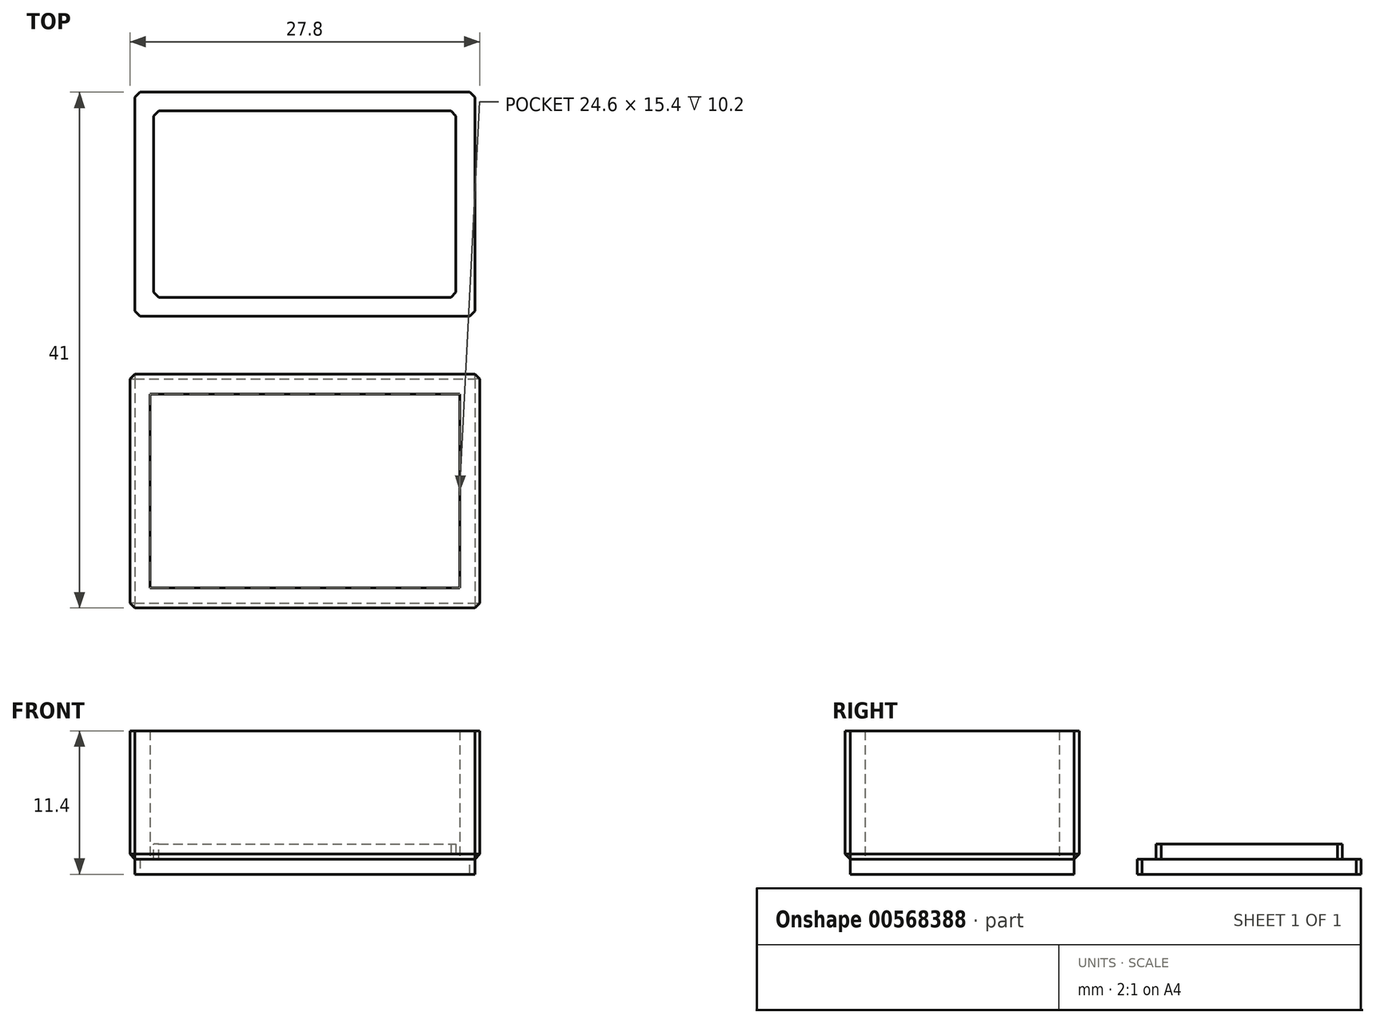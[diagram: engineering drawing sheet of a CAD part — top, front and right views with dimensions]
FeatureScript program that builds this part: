
annotation { "Feature Type Name" : "Feature", "Feature Type Description" : "" }
export const myFeature = defineFeature(function(context is Context, id is Id, definition is map)
    precondition{}
    {
        {
            var Q0;
            Q0=qCreatedBy(makeId("Top.planeOp"),FACE);
            var sketch = newSketch(context, id + "F0", { "sketchPlane" : qUnion([Q0])});
            skLineSegment(sketch, "E0.bottom", {"start": v(-13.5, 8.9) * mm, "end": v(13.5, 8.9) * mm});
            skLineSegment(sketch, "E0.top", {"start": v(-13.5, -8.9) * mm, "end": v(13.5, -8.9) * mm});
            skLineSegment(sketch, "E0.left", {"start": v(-13.5, 8.9) * mm, "end": v(-13.5, -8.9) * mm});
            skLineSegment(sketch, "E0.right", {"start": v(13.5, 8.9) * mm, "end": v(13.5, -8.9) * mm});
            skPoint(sketch, "E0.middle", {"position": v(0, 0) * mm});
            skLineSegment(sketch, "E1.bottom", {"start": v(13.5, 13.9) * mm, "end": v(-13.5, 13.9) * mm});
            skLineSegment(sketch, "E1.top", {"start": v(13.5, 31.7) * mm, "end": v(-13.5, 31.7) * mm});
            skLineSegment(sketch, "E1.left", {"start": v(13.5, 13.9) * mm, "end": v(13.5, 31.7) * mm});
            skLineSegment(sketch, "E1.right", {"start": v(-13.5, 13.9) * mm, "end": v(-13.5, 31.7) * mm});
            skPoint(sketch, "E1.middle", {"position": v(0, 22.8) * mm});
            skSolve(sketch);
        }
        {
            var Q0;
            Q0 = qSketchRegion(id + "F0", true);
            extrude(context, id + "F1", {"entities" : qUnion([Q0]), "depth" : 1.2 * mm, "offsetDistance" : 25 * mm});
        }
        {
            var Q0;
            Q0=makeQuery(id+"F1.opExtrude","CAP_FACE",FACE,{"disambiguationData":[OSD([sQuery(id+"F0.wireOp",EDGE,"E0.bottom"),sQuery(id+"F0.wireOp",EDGE,"E0.top"),sQuery(id+"F0.wireOp",EDGE,"E0.left"),sQuery(id+"F0.wireOp",EDGE,"E0.right")])],"isStart":false});
            var sketch = newSketch(context, id + "F2", { "sketchPlane" : qUnion([Q0])});
            skLineSegment(sketch, "E2.bottom", {"start": v(-12.3, 7.7) * mm, "end": v(12.3, 7.7) * mm});
            skLineSegment(sketch, "E2.top", {"start": v(-12.3, -7.7) * mm, "end": v(12.3, -7.7) * mm});
            skLineSegment(sketch, "E2.left", {"start": v(-12.3, 7.7) * mm, "end": v(-12.3, -7.7) * mm});
            skLineSegment(sketch, "E2.right", {"start": v(12.3, 7.7) * mm, "end": v(12.3, -7.7) * mm});
            skPoint(sketch, "E2.middle", {"position": v(0, 0) * mm});
            skLineSegment(sketch, "E3.bottom", {"start": v(-13.5, 8.9) * mm, "end": v(13.5, 8.9) * mm});
            skLineSegment(sketch, "E3.top", {"start": v(-13.5, -8.9) * mm, "end": v(13.5, -8.9) * mm});
            skLineSegment(sketch, "E3.left", {"start": v(-13.5, 8.9) * mm, "end": v(-13.5, -8.9) * mm});
            skLineSegment(sketch, "E3.right", {"start": v(13.5, 8.9) * mm, "end": v(13.5, -8.9) * mm});
            skLineSegment(sketch, "E4.bottom", {"start": v(-13.9, 9.3) * mm, "end": v(13.9, 9.3) * mm});
            skLineSegment(sketch, "E4.top", {"start": v(-13.9, -9.3) * mm, "end": v(13.9, -9.3) * mm});
            skLineSegment(sketch, "E4.left", {"start": v(-13.9, 9.3) * mm, "end": v(-13.9, -9.3) * mm});
            skLineSegment(sketch, "E4.right", {"start": v(13.9, 9.3) * mm, "end": v(13.9, -9.3) * mm});
            skSolve(sketch);
        }
        {
            var Q0;
            Q0=makeQuery(id+"F2.imprint","IMPRINT",FACE,{"disambiguationData":[TD([[makeQuery(id+"F2.imprint","IMPRINT",EDGE,{"derivedFrom":sQuery(id+"F2.wireOp",EDGE,"E2.bottom")}),1.0]])]});
            var Q1;
            Q1=makeQuery(id+"F2.imprint","IMPRINT",FACE,{"disambiguationData":[TD([[makeQuery(id+"F2.imprint","IMPRINT",EDGE,{"derivedFrom":sQuery(id+"F2.wireOp",EDGE,"E3.bottom")}),1.0]])]});
            extrude(context, id + "F3", {"entities" : qUnion([Q0, Q1]), "operationType" : NewBodyOperationType.ADD, "depth" : 10.2 * mm, "offsetDistance" : 25 * mm});
        }
        {
            var Q0;
            Q0=makeQuery(id+"F1.opExtrude","CAP_FACE",FACE,{"disambiguationData":[OSD([sQuery(id+"F0.wireOp",EDGE,"E1.bottom"),sQuery(id+"F0.wireOp",EDGE,"E1.top"),sQuery(id+"F0.wireOp",EDGE,"E1.left"),sQuery(id+"F0.wireOp",EDGE,"E1.right")])],"isStart":false});
            var sketch = newSketch(context, id + "F4", { "sketchPlane" : qUnion([Q0])});
            skLineSegment(sketch, "E5.bottom", {"start": v(-12, 30.2) * mm, "end": v(12, 30.2) * mm});
            skLineSegment(sketch, "E5.top", {"start": v(-12, 15.4) * mm, "end": v(12, 15.4) * mm});
            skLineSegment(sketch, "E5.left", {"start": v(-12, 30.2) * mm, "end": v(-12, 15.4) * mm});
            skLineSegment(sketch, "E5.right", {"start": v(12, 30.2) * mm, "end": v(12, 15.4) * mm});
            skPoint(sketch, "E5.middle", {"position": v(0, 22.8) * mm});
            skSolve(sketch);
        }
        {
            var Q0;
            Q0=makeQuery(id+"F4.imprint","IMPRINT",FACE,{"disambiguationData":[TD([[makeQuery(id+"F4.imprint","IMPRINT",EDGE,{"derivedFrom":sQuery(id+"F4.wireOp",EDGE,"E5.bottom")}),-1.0]])]});
            extrude(context, id + "F5", {"entities" : qUnion([Q0]), "operationType" : NewBodyOperationType.ADD, "depth" : 1.2 * mm, "offsetDistance" : 25 * mm});
        }
        {
            var Q0;
            Q0=makeQuery(id+"F3.opExtrude","CAP_EDGE",EDGE,{"disambiguationData":[OSD([sQuery(id+"F2.wireOp",EDGE,"E4.left")])],"isStart":true});
            var Q1;
            Q1=makeQuery(id+"F3.opExtrude","SWEPT_EDGE",EDGE,{"disambiguationData":[OSD([sQuery(id+"F2.wireOp",EDGE,"E4.top"),sQuery(id+"F2.wireOp",EDGE,"E4.left")])]});
            var Q2;
            Q2=makeQuery(id+"F3.opExtrude","SWEPT_EDGE",EDGE,{"disambiguationData":[OSD([sQuery(id+"F2.wireOp",EDGE,"E4.bottom"),sQuery(id+"F2.wireOp",EDGE,"E4.left")])]});
            var Q3;
            Q3=makeQuery(id+"F3.opExtrude","SWEPT_EDGE",EDGE,{"disambiguationData":[OSD([sQuery(id+"F2.wireOp",EDGE,"E4.top"),sQuery(id+"F2.wireOp",EDGE,"E4.right")])]});
            var Q4;
            Q4=makeQuery(id+"F3.opExtrude","CAP_EDGE",EDGE,{"disambiguationData":[OSD([sQuery(id+"F2.wireOp",EDGE,"E4.right")])],"isStart":true});
            var Q5;
            Q5=makeQuery(id+"F3.opExtrude","SWEPT_EDGE",EDGE,{"disambiguationData":[OSD([sQuery(id+"F2.wireOp",EDGE,"E4.bottom"),sQuery(id+"F2.wireOp",EDGE,"E4.right")])]});
            var Q6;
            Q6=makeQuery(id+"F1.opExtrude","SWEPT_EDGE",EDGE,{"disambiguationData":[OSD([sQuery(id+"F0.wireOp",EDGE,"E1.top"),sQuery(id+"F0.wireOp",EDGE,"E1.left")])]});
            var Q7;
            Q7=makeQuery(id+"F5.opExtrude","SWEPT_EDGE",EDGE,{"disambiguationData":[OSD([sQuery(id+"F4.wireOp",EDGE,"E5.bottom"),sQuery(id+"F4.wireOp",EDGE,"E5.right")])]});
            var Q8;
            Q8=makeQuery(id+"F5.opExtrude","SWEPT_EDGE",EDGE,{"disambiguationData":[OSD([sQuery(id+"F4.wireOp",EDGE,"E5.top"),sQuery(id+"F4.wireOp",EDGE,"E5.right")])]});
            var Q9;
            Q9=makeQuery(id+"F1.opExtrude","SWEPT_EDGE",EDGE,{"disambiguationData":[OSD([sQuery(id+"F0.wireOp",EDGE,"E1.bottom"),sQuery(id+"F0.wireOp",EDGE,"E1.left")])]});
            var Q10;
            Q10=makeQuery(id+"F1.opExtrude","SWEPT_EDGE",EDGE,{"disambiguationData":[OSD([sQuery(id+"F0.wireOp",EDGE,"E1.top"),sQuery(id+"F0.wireOp",EDGE,"E1.right")])]});
            var Q11;
            Q11=makeQuery(id+"F5.opExtrude","SWEPT_EDGE",EDGE,{"disambiguationData":[OSD([sQuery(id+"F4.wireOp",EDGE,"E5.bottom"),sQuery(id+"F4.wireOp",EDGE,"E5.left")])]});
            var Q12;
            Q12=makeQuery(id+"F1.opExtrude","SWEPT_EDGE",EDGE,{"disambiguationData":[OSD([sQuery(id+"F0.wireOp",EDGE,"E1.bottom"),sQuery(id+"F0.wireOp",EDGE,"E1.right")])]});
            var Q13;
            Q13=makeQuery(id+"F5.opExtrude","SWEPT_EDGE",EDGE,{"disambiguationData":[OSD([sQuery(id+"F4.wireOp",EDGE,"E5.top"),sQuery(id+"F4.wireOp",EDGE,"E5.left")])]});
            var Q14;
            Q14=makeQuery(id+"F3.opExtrude","CAP_EDGE",EDGE,{"disambiguationData":[OSD([sQuery(id+"F2.wireOp",EDGE,"E4.bottom")])],"isStart":true});
            var Q15;
            Q15=makeQuery(id+"F3.opExtrude","CAP_EDGE",EDGE,{"disambiguationData":[OSD([sQuery(id+"F2.wireOp",EDGE,"E4.top")])],"isStart":true});
            chamfer(context, id + "F6", {"entities" : qUnion([Q0, Q1, Q2, Q3, Q4, Q5, Q6, Q7, Q8, Q9, Q10, Q11, Q12, Q13, Q14, Q15]), "width" : .4 * mm, "tangentPropagation" : true});
        }
    });
